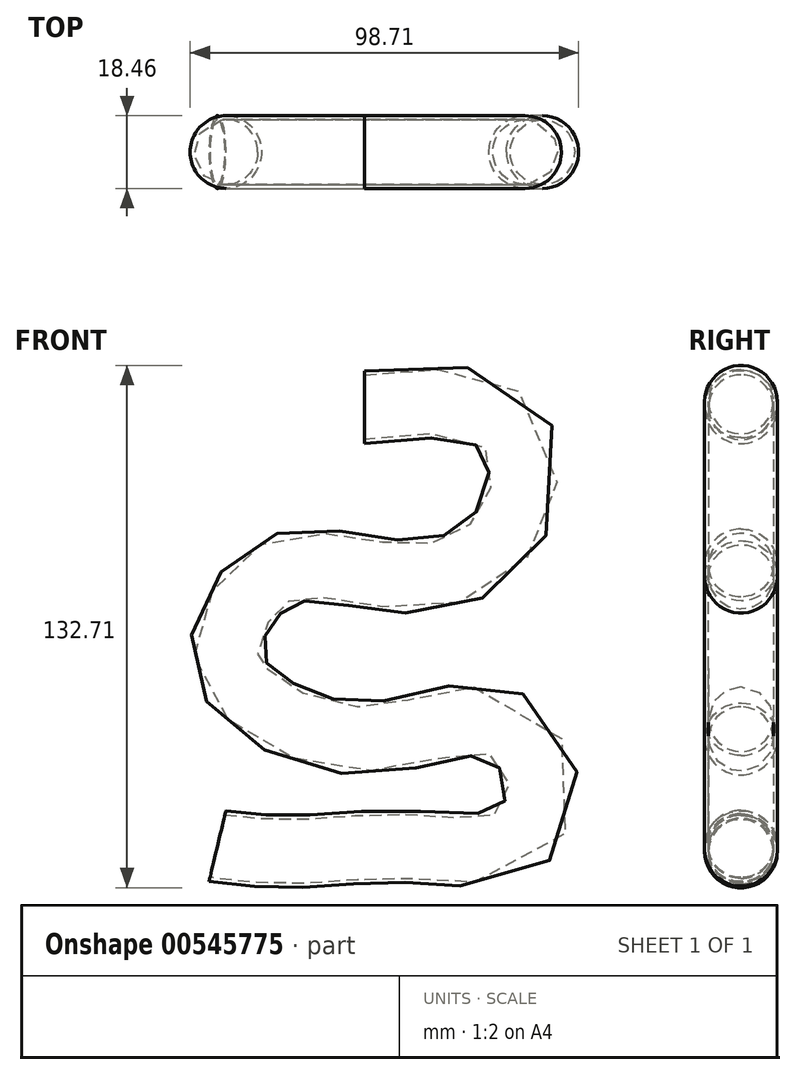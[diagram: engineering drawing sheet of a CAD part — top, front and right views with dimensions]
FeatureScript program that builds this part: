
annotation { "Feature Type Name" : "Feature", "Feature Type Description" : "" }
export const myFeature = defineFeature(function(context is Context, id is Id, definition is map)
    precondition{}
    {
        {
            var Q0;
            Q0=qCreatedBy(makeId("Right.planeOp"),FACE);
            var sketch = newSketch(context, id + "F0", { "sketchPlane" : qUnion([Q0])});
            skCircle(sketch, "E0", {"center": v(-33.68, 40.66) * mm, "radius": 9.23 * mm});
            skSolve(sketch);
        }
        {
            var Q0;
            Q0=qCreatedBy(makeId("Front.planeOp"),FACE);
            var sketch = newSketch(context, id + "F1", { "sketchPlane" : qUnion([Q0])});
            skFitSpline(sketch, "E1", {"points": [v(0, 33.68) * mm, v(31.63, 31.22) * mm, v(30.4, 13.14) * mm, v(11.09, 4.52) * mm, v(-23.41, 5.75) * mm, v(-41.48, -25.88) * mm, v(0, -50.52) * mm, v(33.27, -46.82) * mm, v(36.97, -61.6) * mm, v(11.5, -64.07) * mm, v(-17.66, -65.3) * mm, v(-35.73, -64.07) * mm], "startDerivative": vector(411.6, 47.87) * mm, "endDerivative": vector(-233.7, 27.91) * mm});
            skSolve(sketch);
        }
        {
            var Q0;
            Q0=makeQuery(id+"F0.imprint","IMPRINT",FACE,{"disambiguationData":[TD([[makeQuery(id+"F0.imprint","IMPRINT",EDGE,{"derivedFrom":sQuery(id+"F0.wireOp",EDGE,"E0")}),1.0]])]});
            var Q1;
            Q1=sQuery(id+"F1.wireOp",EDGE,"E1");
            sweep(context, id + "F2", {"profiles" : qUnion([Q0]), "path" : qUnion([Q1])});
        }
        {
            var Q0;
            Q0=makeQuery(id+"F2.opSweep","CAP_FACE",FACE,{"disambiguationData":[OSD([sQuery(id+"F0.wireOp",EDGE,"E0"),sQuery(id+"F1.wireOp",VERTEX,"E1.start")])],"isStart":true});
            var Q1;
            Q1=makeQuery(id+"F2.opSweep","CAP_FACE",FACE,{"disambiguationData":[OSD([sQuery(id+"F0.wireOp",EDGE,"E0"),sQuery(id+"F1.wireOp",VERTEX,"E1.end")])],"isStart":false});
            shell(context, id + "F3", {"entities" : qUnion([Q0, Q1]), "thickness" : 1 * mm});
        }
    });
